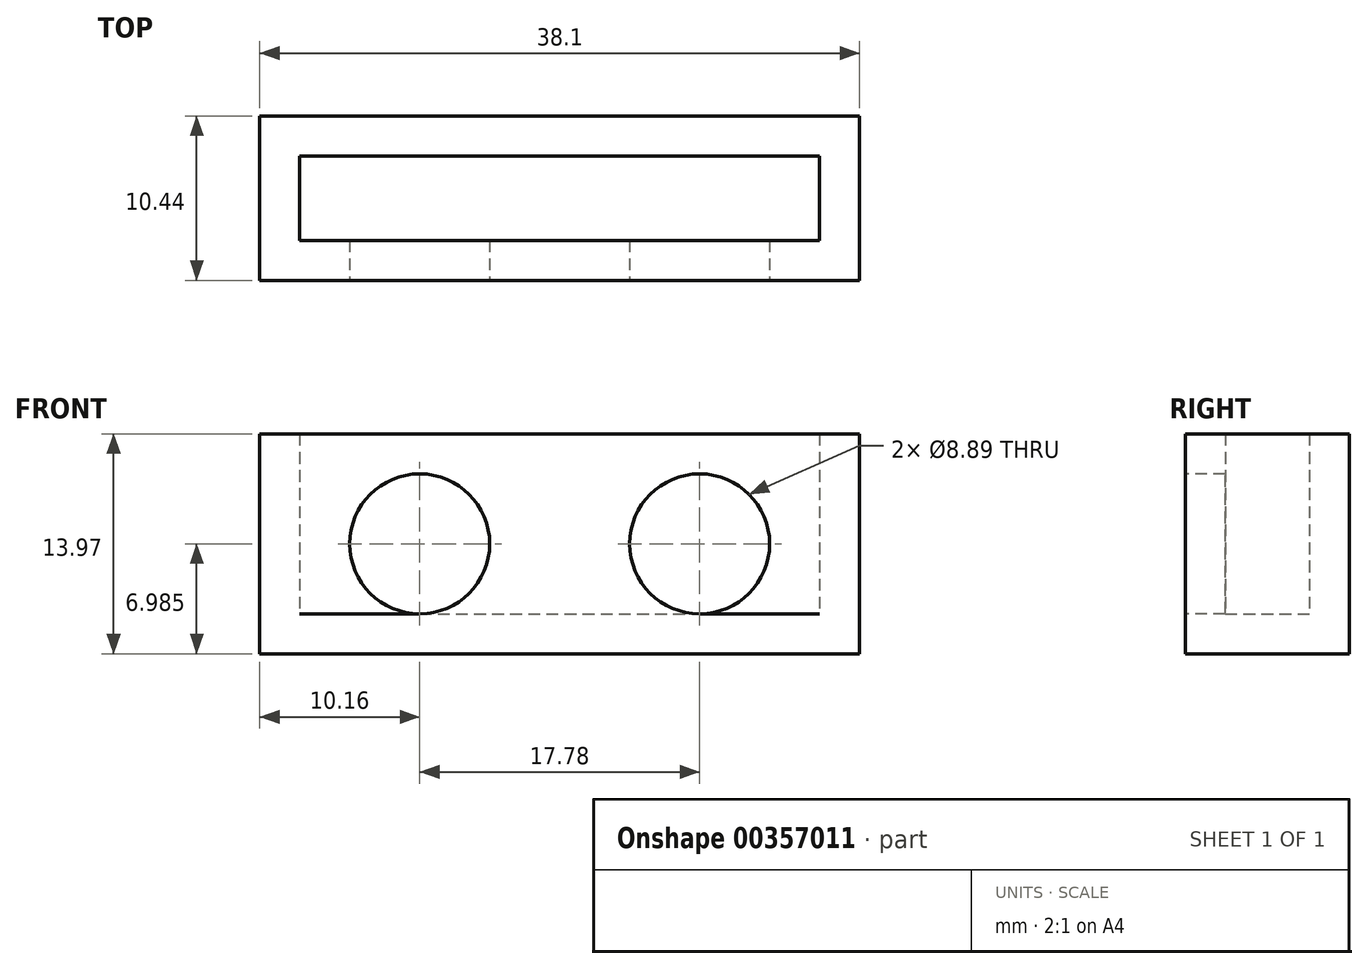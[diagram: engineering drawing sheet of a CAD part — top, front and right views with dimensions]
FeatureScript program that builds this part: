
annotation { "Feature Type Name" : "Feature", "Feature Type Description" : "" }
export const myFeature = defineFeature(function(context is Context, id is Id, definition is map)
    precondition{}
    {
        {
            var Q0;
            Q0=qCreatedBy(makeId("Top.planeOp"),FACE);
            var sketch = newSketch(context, id + "F0", { "sketchPlane" : qUnion([Q0])});
            skLineSegment(sketch, "E0.bottom", {"start": v(-19.05, -5.22) * mm, "end": v(19.05, -5.22) * mm});
            skLineSegment(sketch, "E0.top", {"start": v(-19.05, 5.22) * mm, "end": v(19.05, 5.22) * mm});
            skLineSegment(sketch, "E0.left", {"start": v(-19.05, -5.22) * mm, "end": v(-19.05, 5.22) * mm});
            skLineSegment(sketch, "E0.right", {"start": v(19.05, -5.22) * mm, "end": v(19.05, 5.22) * mm});
            skPoint(sketch, "E0.middle", {"position": v(0, 0) * mm});
            skSolve(sketch);
        }
        {
            var Q0;
            Q0=qSketchRegion(id+"F0",true);
            extrude(context, id + "F1", {"entities" : qUnion([Q0]), "depth" : 13.97 * mm});
        }
        {
            var Q0;
            Q0=makeQuery(id+"F1.opExtrude","CAP_FACE",FACE,{"disambiguationData":[OSD([sQuery(id+"F0.wireOp",EDGE,"E0.bottom"),sQuery(id+"F0.wireOp",EDGE,"E0.top"),sQuery(id+"F0.wireOp",EDGE,"E0.left"),sQuery(id+"F0.wireOp",EDGE,"E0.right")])],"isStart":false});
            shell(context, id + "F2", {"entities" : qUnion([Q0]), "thickness" : 2.54 * mm});
        }
        {
            var Q0;
            Q0=makeQuery(id+"F1.opExtrude","SWEPT_FACE",FACE,{"disambiguationData":[OSD([sQuery(id+"F0.wireOp",EDGE,"E0.bottom")])]});
            var sketch = newSketch(context, id + "F3", { "sketchPlane" : qUnion([Q0])});
            skPoint(sketch, "E1.centerSnap0", {"position": v(-19.05, 6.99) * mm});
            skCircle(sketch, "E2", {"center": v(8.89, 6.99) * mm, "radius": 5.08 * mm});
            skPoint(sketch, "E2.centerSnap0", {"position": v(19.05, 6.99) * mm});
            skCircle(sketch, "E3", {"center": v(-8.89, 6.99) * mm, "radius": 5.08 * mm});
            skSolve(sketch);
        }
        {
            var Q0;
            Q0=sQuery(id+"F3.wireOp",VERTEX,"E3.center");
            var Q1;
            Q1=sQuery(id+"F3.wireOp",VERTEX,"E2.center");
            var Q2;
            Q2=makeQuery(id+"F1.opExtrude","SWEPT_BODY",BODY,{"disambiguationData":[OSD([sQuery(id+"F0.wireOp",EDGE,"E0.bottom"),sQuery(id+"F0.wireOp",EDGE,"E0.top"),sQuery(id+"F0.wireOp",EDGE,"E0.left"),sQuery(id+"F0.wireOp",EDGE,"E0.right")])]});
            hole(context, id + "F4", {"style" : HoleStyle.SIMPLE, "endStyle" : HoleEndStyle.BLIND, "holeDiameter" : 8.9 * mm, "holeDepth" : 2.54 * mm, "tappedDepth" : 12.7 * mm, "tapClearance" : 3, "locations" : qUnion([Q0, Q1]), "scope" : qUnion([Q2])});
        }
    });
